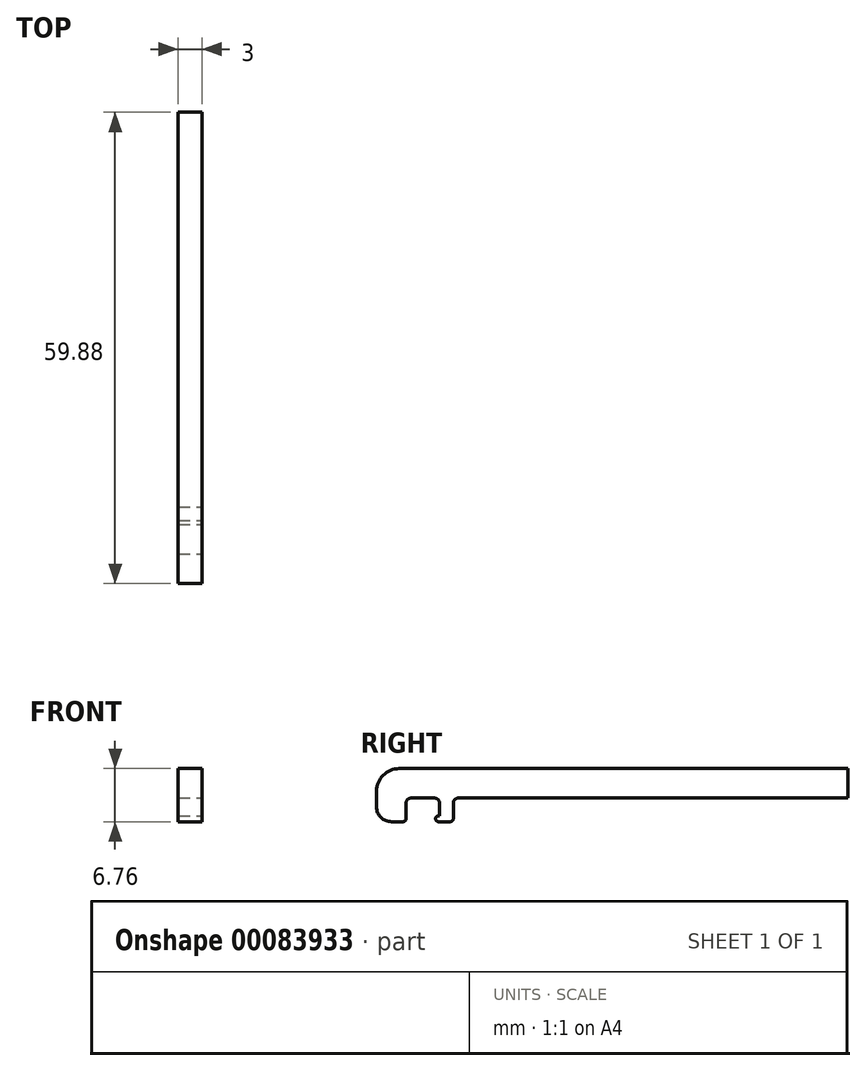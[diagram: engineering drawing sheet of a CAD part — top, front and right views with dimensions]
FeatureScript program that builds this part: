
annotation { "Feature Type Name" : "Feature", "Feature Type Description" : "" }
export const myFeature = defineFeature(function(context is Context, id is Id, definition is map)
    precondition{}
    {
        {
            var Q0;
            Q0=qCreatedBy(makeId("Right.planeOp"),FACE);
            var sketch = newSketch(context, id + "F0", { "sketchPlane" : qUnion([Q0])});
            skLineSegment(sketch, "E0.bottom", {"start": v(0, 0) * mm, "end": v(-60, 0) * mm});
            skLineSegment(sketch, "E0.top", {"start": v(0, 4) * mm, "end": v(-57, 4) * mm});
            skLineSegment(sketch, "E0.left", {"start": v(0, 0) * mm, "end": v(0, 4) * mm});
            skLineSegment(sketch, "E0.right", {"start": v(-60, 0) * mm, "end": v(-60, 1) * mm});
            skLineSegment(sketch, "E1.bottom", {"start": v(-60, 0) * mm, "end": v(-56, 0) * mm});
            skLineSegment(sketch, "E1.top", {"start": v(-58, -3) * mm, "end": v(-56.5, -3) * mm});
            skLineSegment(sketch, "E1.left", {"start": v(-60, 0) * mm, "end": v(-60, -1) * mm});
            skLineSegment(sketch, "E1.right", {"start": v(-56, 0) * mm, "end": v(-56, -2.5) * mm});
            skLineSegment(sketch, "E2.bottom", {"start": v(-52, 0) * mm, "end": v(-50, 0) * mm});
            skLineSegment(sketch, "E2.top", {"start": v(-52, -2) * mm, "end": v(-50, -2) * mm});
            skLineSegment(sketch, "E2.left", {"start": v(-52, 0) * mm, "end": v(-52, -2) * mm});
            skLineSegment(sketch, "E2.right", {"start": v(-50, 0) * mm, "end": v(-50, -2) * mm});
            skPoint(sketch, "E3.visualSharp", {"position": v(-60, -3) * mm});
            skArc(sketch, "E3.filletArc", {"start": v(-60, -1) * mm, "mid": v(-59.41, -2.41) * mm, "end": v(-58, -3) * mm});
            skLineSegment(sketch, "E4.top", {"start": v(-52, -3) * mm, "end": v(-50.5, -3) * mm});
            skLineSegment(sketch, "E4.left", {"start": v(-52, -2) * mm, "end": v(-52, -3) * mm});
            skLineSegment(sketch, "E4.right", {"start": v(-50, -2) * mm, "end": v(-50, -2.5) * mm});
            skArc(sketch, "E5", {"start": v(-52, -2) * mm, "mid": v(-52.5, -2.5) * mm, "end": v(-52, -3) * mm});
            skPoint(sketch, "E6.visualSharp", {"position": v(-56, -3) * mm});
            skArc(sketch, "E6.filletArc", {"start": v(-56.5, -3) * mm, "mid": v(-56.15, -2.85) * mm, "end": v(-56, -2.5) * mm});
            skPoint(sketch, "E7.visualSharp", {"position": v(-50, -3) * mm});
            skArc(sketch, "E7.filletArc", {"start": v(-50.5, -3) * mm, "mid": v(-50.15, -2.85) * mm, "end": v(-50, -2.5) * mm});
            skPoint(sketch, "E8.visualSharp", {"position": v(-60, 4) * mm});
            skArc(sketch, "E8.filletArc", {"start": v(-57, 4) * mm, "mid": v(-59.12, 3.12) * mm, "end": v(-60, 1) * mm});
            skSolve(sketch);
        }
        {
            var Q0;
            Q0=qSketchRegion(id+"F0",true);
            extrude(context, id + "F1", {"entities" : qUnion([Q0]), "endBound" : BoundingType.SYMMETRIC, "depth" : 3 * mm});
        }
        {
            var Q0;
            Q0=makeQuery(id+"F1.opExtrude","SWEPT_EDGE",EDGE,{"disambiguationData":[OSD([sQuery(id+"F0.wireOp",EDGE,"E0.bottom"),sQuery(id+"F0.wireOp",EDGE,"E1.bottom"),sQuery(id+"F0.wireOp",EDGE,"E1.right")])]});
            var Q1;
            Q1=makeQuery(id+"F1.opExtrude","SWEPT_EDGE",EDGE,{"disambiguationData":[OSD([sQuery(id+"F0.wireOp",EDGE,"E0.bottom"),sQuery(id+"F0.wireOp",EDGE,"E2.bottom"),sQuery(id+"F0.wireOp",EDGE,"E2.left")])]});
            var Q2;
            Q2=makeQuery(id+"F1.opExtrude","SWEPT_EDGE",EDGE,{"disambiguationData":[OSD([sQuery(id+"F0.wireOp",EDGE,"E0.bottom"),sQuery(id+"F0.wireOp",EDGE,"E2.bottom"),sQuery(id+"F0.wireOp",EDGE,"E2.right")])]});
            fillet(context, id + "F2", {"entities" : qUnion([Q0, Q1, Q2]), "radius" : .5 * mm, "tangentPropagation" : true, "allowEdgeOverflow" : false});
        }
        {
            var Q0;
            Q0=makeQuery(id+"F1.opExtrude","SWEPT_BODY",BODY,{"disambiguationData":[OSD([sQuery(id+"F0.wireOp",EDGE,"E0.bottom"),sQuery(id+"F0.wireOp",EDGE,"E0.top"),sQuery(id+"F0.wireOp",EDGE,"E0.left"),sQuery(id+"F0.wireOp",EDGE,"E0.right"),sQuery(id+"F0.wireOp",EDGE,"E1.top"),sQuery(id+"F0.wireOp",EDGE,"E1.left"),sQuery(id+"F0.wireOp",EDGE,"E1.right"),sQuery(id+"F0.wireOp",EDGE,"E2.left"),sQuery(id+"F0.wireOp",EDGE,"E2.right"),sQuery(id+"F0.wireOp",EDGE,"E3.filletArc"),sQuery(id+"F0.wireOp",EDGE,"E4.top"),sQuery(id+"F0.wireOp",EDGE,"E4.right"),sQuery(id+"F0.wireOp",EDGE,"E5"),sQuery(id+"F0.wireOp",EDGE,"E6.filletArc"),sQuery(id+"F0.wireOp",EDGE,"E7.filletArc"),sQuery(id+"F0.wireOp",EDGE,"E8.filletArc")])]});
            var Q1;
            Q1=makeQuery(id+"F1.opExtrude","SWEPT_FACE",FACE,{"disambiguationData":[OSD([sQuery(id+"F0.wireOp",EDGE,"E0.left")])]});
            mirror(context, id + "F3", {"operationType" : NewBodyOperationType.ADD, "entities" : qUnion([Q0]), "mirrorPlane" : qUnion([Q1])});
        }
        {
            var Q0;
            {var subQ0=makeQuery(id+"F1.opExtrude","CAP_FACE",FACE,{"disambiguationData":[OSD([sQuery(id+"F0.wireOp",EDGE,"E0.bottom"),sQuery(id+"F0.wireOp",EDGE,"E0.top"),sQuery(id+"F0.wireOp",EDGE,"E0.left"),sQuery(id+"F0.wireOp",EDGE,"E0.right"),sQuery(id+"F0.wireOp",EDGE,"E1.top"),sQuery(id+"F0.wireOp",EDGE,"E1.left"),sQuery(id+"F0.wireOp",EDGE,"E1.right"),sQuery(id+"F0.wireOp",EDGE,"E2.left"),sQuery(id+"F0.wireOp",EDGE,"E2.right"),sQuery(id+"F0.wireOp",EDGE,"E3.filletArc"),sQuery(id+"F0.wireOp",EDGE,"E4.top"),sQuery(id+"F0.wireOp",EDGE,"E4.right"),sQuery(id+"F0.wireOp",EDGE,"E5"),sQuery(id+"F0.wireOp",EDGE,"E6.filletArc"),sQuery(id+"F0.wireOp",EDGE,"E7.filletArc"),sQuery(id+"F0.wireOp",EDGE,"E8.filletArc")])],"isStart":false});Q0=makeQuery(id+"F3.boolean.opBoolean","MERGE",FACE,{"derivedFrom":[subQ0,makeQuery(id+"F3.opPattern","COPY",FACE,{"derivedFrom":subQ0,"instanceName":"1"})]});}
            var sketch = newSketch(context, id + "F4", { "sketchPlane" : qUnion([Q0])});
            skArc(sketch, "E9.0", {"start": v(-57, 4) * mm, "mid": v(-59.12, 3.12) * mm, "end": v(-60, 1) * mm});
            skLineSegment(sketch, "E10.0", {"start": v(57, 4) * mm, "end": v(-57, 4) * mm});
            skLineSegment(sketch, "E11.0", {"start": v(-60, 1) * mm, "end": v(-60, -1) * mm});
            skArc(sketch, "E12.0", {"start": v(-60, -1) * mm, "mid": v(-59.41, -2.41) * mm, "end": v(-58, -3) * mm});
            skLineSegment(sketch, "E13.0", {"start": v(-58, -3) * mm, "end": v(-56.5, -3) * mm});
            skArc(sketch, "E14.0", {"start": v(-56.5, -3) * mm, "mid": v(-56.15, -2.85) * mm, "end": v(-56, -2.5) * mm});
            skLineSegment(sketch, "E15.0", {"start": v(-56, -0.5) * mm, "end": v(-56, -2.5) * mm});
            skArc(sketch, "E16.0", {"start": v(-56, -0.5) * mm, "mid": v(-55.85, -0.15) * mm, "end": v(-55.5, 0) * mm});
            skLineSegment(sketch, "E17.0", {"start": v(-52.5, 0) * mm, "end": v(-55.5, 0) * mm});
            skArc(sketch, "E18.0", {"start": v(-52.5, 0) * mm, "mid": v(-52.15, -0.15) * mm, "end": v(-52, -0.5) * mm});
            skLineSegment(sketch, "E19.0", {"start": v(-52, -0.5) * mm, "end": v(-52, -2) * mm});
            skArc(sketch, "E20.0", {"start": v(-52, -2) * mm, "mid": v(-52.5, -2.5) * mm, "end": v(-52, -3) * mm});
            skLineSegment(sketch, "E21.0", {"start": v(-52, -3) * mm, "end": v(-50.5, -3) * mm});
            skArc(sketch, "E22.0", {"start": v(-50.5, -3) * mm, "mid": v(-50.15, -2.85) * mm, "end": v(-50, -2.5) * mm});
            skLineSegment(sketch, "E23.0", {"start": v(-50, -0.5) * mm, "end": v(-50, -2.5) * mm});
            skArc(sketch, "E24.0", {"start": v(-50, -0.5) * mm, "mid": v(-49.85, -0.15) * mm, "end": v(-49.5, 0) * mm});
            skLineSegment(sketch, "E25.0", {"start": v(49.5, 0) * mm, "end": v(-49.5, 0) * mm});
            skLineSegment(sketch, "E26.0", {"start": v(49.5, 0.13) * mm, "end": v(-49.5, 0.13) * mm});
            skArc(sketch, "E26.1", {"start": v(-50.12, -0.5) * mm, "mid": v(-49.94, -0.06) * mm, "end": v(-49.5, 0.13) * mm});
            skLineSegment(sketch, "E26.2", {"start": v(-50.12, -0.5) * mm, "end": v(-50.12, -2.5) * mm});
            skArc(sketch, "E26.3", {"start": v(-50.5, -2.88) * mm, "mid": v(-50.23, -2.77) * mm, "end": v(-50.12, -2.5) * mm});
            skLineSegment(sketch, "E26.4", {"start": v(-52, -2.88) * mm, "end": v(-50.5, -2.88) * mm});
            skArc(sketch, "E26.5", {"start": v(-51.87, -2.15) * mm, "mid": v(-52.37, -2.44) * mm, "end": v(-52, -2.88) * mm});
            skLineSegment(sketch, "E26.6", {"start": v(-51.87, -0.5) * mm, "end": v(-51.87, -2.15) * mm});
            skArc(sketch, "E26.7", {"start": v(-59.88, -1) * mm, "mid": v(-59.33, -2.33) * mm, "end": v(-58, -2.88) * mm});
            skLineSegment(sketch, "E26.8", {"start": v(-59.88, 1) * mm, "end": v(-59.88, -1) * mm});
            skArc(sketch, "E26.9", {"start": v(-57, 3.88) * mm, "mid": v(-59.03, 3.03) * mm, "end": v(-59.88, 1) * mm});
            skLineSegment(sketch, "E26.10", {"start": v(57, 3.88) * mm, "end": v(-57, 3.88) * mm});
            skLineSegment(sketch, "E26.11", {"start": v(-58, -2.88) * mm, "end": v(-56.5, -2.88) * mm});
            skArc(sketch, "E26.12", {"start": v(-56.5, -2.88) * mm, "mid": v(-56.23, -2.77) * mm, "end": v(-56.12, -2.5) * mm});
            skLineSegment(sketch, "E26.13", {"start": v(-56.12, -0.5) * mm, "end": v(-56.12, -2.5) * mm});
            skArc(sketch, "E26.14", {"start": v(-56.12, -0.5) * mm, "mid": v(-55.94, -0.06) * mm, "end": v(-55.5, 0.13) * mm});
            skLineSegment(sketch, "E26.15", {"start": v(-52.5, 0.13) * mm, "end": v(-55.5, 0.13) * mm});
            skArc(sketch, "E26.16", {"start": v(-52.5, 0.13) * mm, "mid": v(-52.06, -0.06) * mm, "end": v(-51.87, -0.5) * mm});
            skLineSegment(sketch, "E27.0", {"start": v(49.5, -4.88) * mm, "end": v(-45.68, -4.88) * mm});
            skArc(sketch, "E27.1", {"start": v(-50.5, -7.88) * mm, "mid": v(-47.66, -7.06) * mm, "end": v(-45.68, -4.87) * mm});
            skLineSegment(sketch, "E27.2", {"start": v(-52, -7.88) * mm, "end": v(-50.5, -7.88) * mm});
            skArc(sketch, "E27.3", {"start": v(-54.25, -7.38) * mm, "mid": v(-53.15, -7.75) * mm, "end": v(-52, -7.88) * mm});
            skArc(sketch, "E27.4", {"start": v(-56.5, -7.88) * mm, "mid": v(-55.35, -7.75) * mm, "end": v(-54.25, -7.38) * mm});
            skLineSegment(sketch, "E27.5", {"start": v(-58, -7.88) * mm, "end": v(-56.5, -7.88) * mm});
            skLineSegment(sketch, "E27.6", {"start": v(57, 8.88) * mm, "end": v(-57, 8.88) * mm});
            skArc(sketch, "E27.7", {"start": v(-57, 8.88) * mm, "mid": v(-62.57, 6.57) * mm, "end": v(-64.87, 1) * mm});
            skLineSegment(sketch, "E27.8", {"start": v(-64.88, 1) * mm, "end": v(-64.88, -1) * mm});
            skArc(sketch, "E27.9", {"start": v(-64.88, -1) * mm, "mid": v(-62.86, -5.86) * mm, "end": v(-58, -7.88) * mm});
            skLineSegment(sketch, "E28", {"start": v(49.5, -4.88) * mm, "end": v(49.5, 0.13) * mm});
            skLineSegment(sketch, "E29", {"start": v(57, 8.88) * mm, "end": v(57, 3.88) * mm});
            skSolve(sketch);
        }
        {
            var Q0;
            Q0=makeQuery(id+"F4.imprint","IMPRINT",FACE,{"disambiguationData":[TD([[makeQuery(id+"F4.imprint","IMPRINT",EDGE,{"derivedFrom":sQuery(id+"F4.wireOp",EDGE,"E9.0")}),1.0]])]});
            extrude(context, id + "F5", {"entities" : qUnion([Q0]), "operationType" : NewBodyOperationType.REMOVE, "endBound" : BoundingType.UP_TO_NEXT, "oppositeDirection" : true, "depth" : 25 * mm});
        }
        {
            var Q0;
            {var subQ0=makeQuery(id+"F1.opExtrude","CAP_FACE",FACE,{"disambiguationData":[OSD([sQuery(id+"F0.wireOp",EDGE,"E0.bottom"),sQuery(id+"F0.wireOp",EDGE,"E0.top"),sQuery(id+"F0.wireOp",EDGE,"E0.left"),sQuery(id+"F0.wireOp",EDGE,"E0.right"),sQuery(id+"F0.wireOp",EDGE,"E1.top"),sQuery(id+"F0.wireOp",EDGE,"E1.left"),sQuery(id+"F0.wireOp",EDGE,"E1.right"),sQuery(id+"F0.wireOp",EDGE,"E2.left"),sQuery(id+"F0.wireOp",EDGE,"E2.right"),sQuery(id+"F0.wireOp",EDGE,"E3.filletArc"),sQuery(id+"F0.wireOp",EDGE,"E4.top"),sQuery(id+"F0.wireOp",EDGE,"E4.right"),sQuery(id+"F0.wireOp",EDGE,"E5"),sQuery(id+"F0.wireOp",EDGE,"E6.filletArc"),sQuery(id+"F0.wireOp",EDGE,"E7.filletArc"),sQuery(id+"F0.wireOp",EDGE,"E8.filletArc")])],"isStart":false});Q0=makeQuery(id+"F3.boolean.opBoolean","MERGE",FACE,{"derivedFrom":[subQ0,makeQuery(id+"F3.opPattern","COPY",FACE,{"derivedFrom":subQ0,"instanceName":"1"})]});}
            var sketch = newSketch(context, id + "F6", { "sketchPlane" : qUnion([Q0])});
            skLineSegment(sketch, "E30.bottom", {"start": v(0, 13.43) * mm, "end": v(70.55, 13.43) * mm});
            skLineSegment(sketch, "E30.top", {"start": v(0, -19.48) * mm, "end": v(70.55, -19.48) * mm});
            skLineSegment(sketch, "E30.left", {"start": v(0, 13.43) * mm, "end": v(0, -19.48) * mm});
            skLineSegment(sketch, "E30.right", {"start": v(70.55, 13.43) * mm, "end": v(70.55, -19.48) * mm});
            skSolve(sketch);
        }
        {
            var Q0;
            Q0 = qSketchRegion(id + "F6", true);
            extrude(context, id + "F7", {"entities" : qUnion([Q0]), "operationType" : NewBodyOperationType.REMOVE, "endBound" : BoundingType.THROUGH_ALL, "oppositeDirection" : true, "depth" : 25 * mm});
        }
    });
